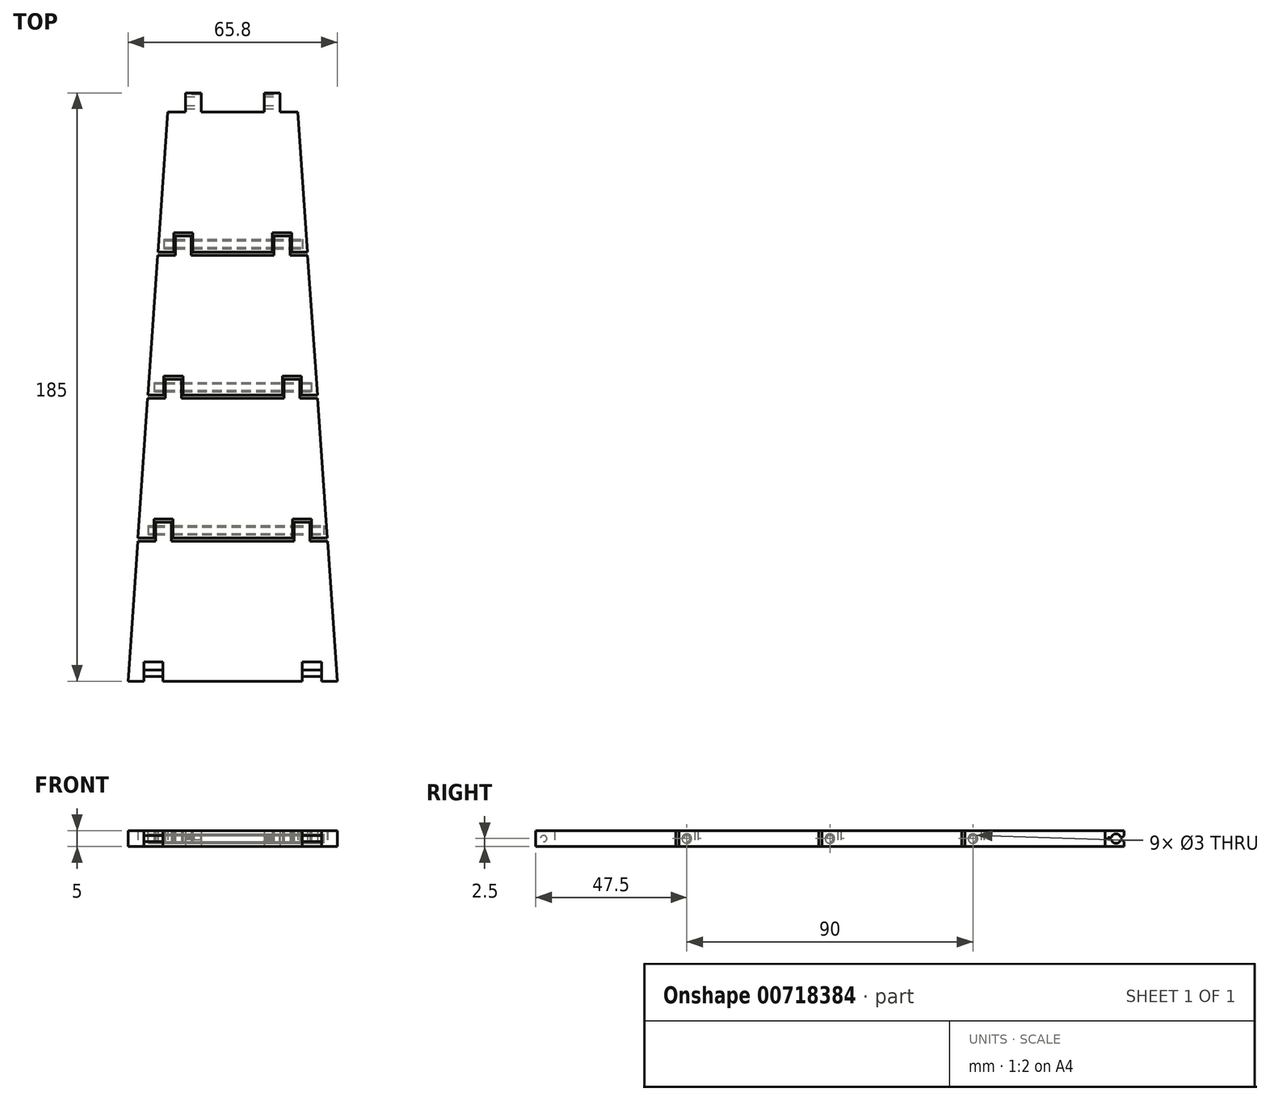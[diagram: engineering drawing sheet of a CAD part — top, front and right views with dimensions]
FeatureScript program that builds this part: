
annotation { "Feature Type Name" : "Feature", "Feature Type Description" : "" }
export const myFeature = defineFeature(function(context is Context, id is Id, definition is map)
    precondition{}
    {
        {
            var Q0;
            Q0=qCreatedBy(makeId("Top.planeOp"),FACE);
            var sketch = newSketch(context, id + "F0", { "sketchPlane" : qUnion([Q0])});
            skLineSegment(sketch, "E0", {"start": v(-23.52, 43.1) * mm, "end": v(-18.52, 43.1) * mm});
            skLineSegment(sketch, "E1", {"start": v(-26.65, -1.9) * mm, "end": v(-21.65, -1.9) * mm});
            skLineSegment(sketch, "E2", {"start": v(-29.78, -46.9) * mm, "end": v(-24.78, -46.9) * mm});
            skLineSegment(sketch, "E3", {"start": v(-32.9, -91.9) * mm, "end": v(-27.9, -91.9) * mm});
            skLineSegment(sketch, "E4.top", {"start": v(-18.52, 49.1) * mm, "end": v(-12.52, 49.1) * mm});
            skLineSegment(sketch, "E4.left", {"start": v(-18.52, 43.1) * mm, "end": v(-18.52, 49.1) * mm});
            skLineSegment(sketch, "E4.right", {"start": v(-12.52, 43.1) * mm, "end": v(-12.52, 49.1) * mm});
            skLineSegment(sketch, "E5.top", {"start": v(-21.65, 4.1) * mm, "end": v(-15.65, 4.1) * mm});
            skLineSegment(sketch, "E5.left", {"start": v(-21.65, -1.9) * mm, "end": v(-21.65, 4.1) * mm});
            skLineSegment(sketch, "E5.right", {"start": v(-15.65, -1.9) * mm, "end": v(-15.65, 4.1) * mm});
            skLineSegment(sketch, "E6.top", {"start": v(-24.78, -40.9) * mm, "end": v(-18.78, -40.9) * mm});
            skLineSegment(sketch, "E6.left", {"start": v(-24.78, -46.9) * mm, "end": v(-24.78, -40.9) * mm});
            skLineSegment(sketch, "E6.right", {"start": v(-18.78, -46.9) * mm, "end": v(-18.78, -40.9) * mm});
            skLineSegment(sketch, "E7.top", {"start": v(-27.9, -85.9) * mm, "end": v(-21.9, -85.9) * mm});
            skLineSegment(sketch, "E7.left", {"start": v(-27.9, -91.9) * mm, "end": v(-27.9, -85.9) * mm});
            skLineSegment(sketch, "E7.right", {"start": v(-21.9, -91.9) * mm, "end": v(-21.9, -85.9) * mm});
            skLineSegment(sketch, "E8.MirrorCS", {"start": v(27.9, -91.9) * mm, "end": v(27.9, -85.9) * mm});
            skLineSegment(sketch, "E9.MirrorCS", {"start": v(27.9, -85.9) * mm, "end": v(21.9, -85.9) * mm});
            skLineSegment(sketch, "E10.MirrorCS", {"start": v(21.9, -91.9) * mm, "end": v(21.9, -85.9) * mm});
            skLineSegment(sketch, "E11.MirrorCS", {"start": v(24.78, -46.9) * mm, "end": v(24.78, -40.9) * mm});
            skLineSegment(sketch, "E12.MirrorCS", {"start": v(18.78, -46.9) * mm, "end": v(18.78, -40.9) * mm});
            skLineSegment(sketch, "E13.MirrorCS", {"start": v(24.78, -40.9) * mm, "end": v(18.78, -40.9) * mm});
            skLineSegment(sketch, "E14.MirrorCS", {"start": v(21.65, 4.1) * mm, "end": v(15.65, 4.1) * mm});
            skLineSegment(sketch, "E15.MirrorCS", {"start": v(21.65, -1.9) * mm, "end": v(21.65, 4.1) * mm});
            skLineSegment(sketch, "E16.MirrorCS", {"start": v(15.65, -1.9) * mm, "end": v(15.65, 4.1) * mm});
            skLineSegment(sketch, "E17.MirrorCS", {"start": v(12.52, 43.1) * mm, "end": v(12.52, 49.1) * mm});
            skLineSegment(sketch, "E18.MirrorCS", {"start": v(18.52, 49.1) * mm, "end": v(12.52, 49.1) * mm});
            skLineSegment(sketch, "E19.MirrorCS", {"start": v(18.52, 43.1) * mm, "end": v(18.52, 49.1) * mm});
            skLineSegment(sketch, "E20", {"start": v(-20.46, 87.1) * mm, "end": v(-14.89, 87.1) * mm});
            skLineSegment(sketch, "E21", {"start": v(-23.59, 42.1) * mm, "end": v(-18.02, 42.1) * mm});
            skLineSegment(sketch, "E22", {"start": v(-26.72, -2.9) * mm, "end": v(-21.15, -2.9) * mm});
            skLineSegment(sketch, "E23", {"start": v(-29.84, -47.9) * mm, "end": v(-24.28, -47.9) * mm});
            skLineSegment(sketch, "E24.top", {"start": v(-14.89, 93.1) * mm, "end": v(-9.89, 93.1) * mm});
            skLineSegment(sketch, "E24.left", {"start": v(-14.89, 87.1) * mm, "end": v(-14.89, 93.1) * mm});
            skLineSegment(sketch, "E24.right", {"start": v(-9.89, 87.1) * mm, "end": v(-9.89, 93.1) * mm});
            skLineSegment(sketch, "E25.top", {"start": v(-18.02, 48.1) * mm, "end": v(-13.02, 48.1) * mm});
            skLineSegment(sketch, "E25.left", {"start": v(-18.02, 42.1) * mm, "end": v(-18.02, 48.1) * mm});
            skLineSegment(sketch, "E25.right", {"start": v(-13.02, 42.1) * mm, "end": v(-13.02, 48.1) * mm});
            skLineSegment(sketch, "E26.top", {"start": v(-21.15, 3.1) * mm, "end": v(-16.15, 3.1) * mm});
            skLineSegment(sketch, "E26.left", {"start": v(-21.15, -2.9) * mm, "end": v(-21.15, 3.1) * mm});
            skLineSegment(sketch, "E26.right", {"start": v(-16.15, -2.9) * mm, "end": v(-16.15, 3.1) * mm});
            skLineSegment(sketch, "E27.top", {"start": v(-24.28, -41.9) * mm, "end": v(-19.28, -41.9) * mm});
            skLineSegment(sketch, "E27.left", {"start": v(-24.28, -47.9) * mm, "end": v(-24.28, -41.9) * mm});
            skLineSegment(sketch, "E27.right", {"start": v(-19.28, -47.9) * mm, "end": v(-19.28, -41.9) * mm});
            skLineSegment(sketch, "E28.MirrorCS", {"start": v(14.89, 93.1) * mm, "end": v(9.89, 93.1) * mm});
            skLineSegment(sketch, "E29.MirrorCS", {"start": v(18.02, 42.1) * mm, "end": v(18.02, 48.1) * mm});
            skLineSegment(sketch, "E30.MirrorCS", {"start": v(18.02, 48.1) * mm, "end": v(13.02, 48.1) * mm});
            skLineSegment(sketch, "E31.MirrorCS", {"start": v(13.02, 42.1) * mm, "end": v(13.02, 48.1) * mm});
            skLineSegment(sketch, "E32.MirrorCS", {"start": v(21.15, -2.9) * mm, "end": v(21.15, 3.1) * mm});
            skLineSegment(sketch, "E33.MirrorCS", {"start": v(21.15, 3.1) * mm, "end": v(16.15, 3.1) * mm});
            skLineSegment(sketch, "E34.MirrorCS", {"start": v(16.15, -2.9) * mm, "end": v(16.15, 3.1) * mm});
            skLineSegment(sketch, "E35.MirrorCS", {"start": v(24.28, -47.9) * mm, "end": v(24.28, -41.9) * mm});
            skLineSegment(sketch, "E36.MirrorCS", {"start": v(24.28, -41.9) * mm, "end": v(19.28, -41.9) * mm});
            skLineSegment(sketch, "E37.MirrorCS", {"start": v(19.28, -47.9) * mm, "end": v(19.28, -41.9) * mm});
            skLineSegment(sketch, "E38.trimOffspring", {"start": v(-20.46, 87.1) * mm, "end": v(-23.52, 43.1) * mm});
            skLineSegment(sketch, "E39.trimOffspring", {"start": v(14.89, 87.1) * mm, "end": v(20.46, 87.1) * mm});
            skLineSegment(sketch, "E40.trimOffspring", {"start": v(20.46, 87.1) * mm, "end": v(23.52, 43.1) * mm});
            skLineSegment(sketch, "E41.trimOffspring", {"start": v(-9.89, 87.1) * mm, "end": v(9.89, 87.1) * mm});
            skLineSegment(sketch, "E42.trimOffspring", {"start": v(-23.59, 42.1) * mm, "end": v(-26.65, -1.9) * mm});
            skLineSegment(sketch, "E43.trimOffspring", {"start": v(-12.52, 43.1) * mm, "end": v(12.52, 43.1) * mm});
            skLineSegment(sketch, "E44.trimOffspring", {"start": v(-13.02, 42.1) * mm, "end": v(13.02, 42.1) * mm});
            skLineSegment(sketch, "E45.trimOffspring", {"start": v(18.52, 43.1) * mm, "end": v(23.52, 43.1) * mm});
            skLineSegment(sketch, "E46.trimOffspring", {"start": v(18.02, 42.1) * mm, "end": v(23.59, 42.1) * mm});
            skLineSegment(sketch, "E47.trimOffspring", {"start": v(23.59, 42.1) * mm, "end": v(26.65, -1.9) * mm});
            skLineSegment(sketch, "E48.trimOffspring", {"start": v(-26.72, -2.9) * mm, "end": v(-29.78, -46.9) * mm});
            skLineSegment(sketch, "E49.trimOffspring", {"start": v(-15.65, -1.9) * mm, "end": v(15.65, -1.9) * mm});
            skLineSegment(sketch, "E50.trimOffspring", {"start": v(-16.15, -2.9) * mm, "end": v(16.15, -2.9) * mm});
            skLineSegment(sketch, "E51.trimOffspring", {"start": v(21.65, -1.9) * mm, "end": v(26.65, -1.9) * mm});
            skLineSegment(sketch, "E52.trimOffspring", {"start": v(21.15, -2.9) * mm, "end": v(26.72, -2.9) * mm});
            skLineSegment(sketch, "E53.trimOffspring", {"start": v(26.72, -2.9) * mm, "end": v(29.78, -46.9) * mm});
            skLineSegment(sketch, "E54.trimOffspring", {"start": v(-29.84, -47.9) * mm, "end": v(-32.9, -91.9) * mm});
            skLineSegment(sketch, "E55.trimOffspring", {"start": v(-18.78, -46.9) * mm, "end": v(18.78, -46.9) * mm});
            skLineSegment(sketch, "E56.trimOffspring", {"start": v(-19.28, -47.9) * mm, "end": v(19.28, -47.9) * mm});
            skLineSegment(sketch, "E57.trimOffspring", {"start": v(24.78, -46.9) * mm, "end": v(29.78, -46.9) * mm});
            skLineSegment(sketch, "E58.trimOffspring", {"start": v(24.28, -47.9) * mm, "end": v(29.84, -47.9) * mm});
            skLineSegment(sketch, "E59.trimOffspring", {"start": v(29.84, -47.9) * mm, "end": v(32.9, -91.9) * mm});
            skLineSegment(sketch, "E60.trimOffspring", {"start": v(-21.9, -91.9) * mm, "end": v(21.9, -91.9) * mm});
            skLineSegment(sketch, "E61.trimOffspring", {"start": v(27.9, -91.9) * mm, "end": v(32.9, -91.9) * mm});
            skLineSegment(sketch, "E62", {"start": v(9.89, 93.1) * mm, "end": v(9.89, 87.1) * mm});
            skLineSegment(sketch, "E63", {"start": v(14.89, 93.1) * mm, "end": v(14.89, 87.1) * mm});
            skSolve(sketch);
        }
        {
            var Q0;
            Q0 = qSketchRegion(id + "F0", true);
            extrude(context, id + "F1", {"entities" : qUnion([Q0]), "depth" : 5 * mm, "offsetDistance" : 25 * mm});
        }
        {
            var Q0;
            Q0=makeQuery(id+"F1.opExtrude","SWEPT_FACE",FACE,{"disambiguationData":[OSD([sQuery(id+"F0.wireOp",EDGE,"E29.MirrorCS")])]});
            cPlane(context, id + "F2", {"entities" : qUnion([Q0]), "cplaneType" : CPlaneType.OFFSET, "offset" : 10 * mm, "width" : 150 * mm, "height" : 150 * mm});
        }
        {
            var Q0;
            Q0=makeQuery(id+"F1.opExtrude","SWEPT_FACE",FACE,{"disambiguationData":[OSD([sQuery(id+"F0.wireOp",EDGE,"E32.MirrorCS")])]});
            cPlane(context, id + "F3", {"entities" : qUnion([Q0]), "cplaneType" : CPlaneType.OFFSET, "offset" : 10 * mm, "width" : 150 * mm, "height" : 150 * mm});
        }
        {
            var Q0;
            Q0=makeQuery(id+"F1.opExtrude","SWEPT_FACE",FACE,{"disambiguationData":[OSD([sQuery(id+"F0.wireOp",EDGE,"E35.MirrorCS")])]});
            cPlane(context, id + "F4", {"entities" : qUnion([Q0]), "cplaneType" : CPlaneType.OFFSET, "offset" : 10 * mm, "width" : 150 * mm, "height" : 150 * mm});
        }
        {
            var Q0;
            Q0=makeQuery(id+"F1.opExtrude","SWEPT_FACE",FACE,{"disambiguationData":[OSD([sQuery(id+"F0.wireOp",EDGE,"E10.MirrorCS")])]});
            cPlane(context, id + "F5", {"entities" : qUnion([Q0]), "cplaneType" : CPlaneType.OFFSET, "offset" : 15 * mm, "width" : 150 * mm, "height" : 150 * mm});
        }
        {
            var Q0;
            Q0=makeQuery(id+"F1.opExtrude","SWEPT_FACE",FACE,{"disambiguationData":[OSD([sQuery(id+"F0.wireOp",EDGE,"E63")])]});
            cPlane(context, id + "F6", {"entities" : qUnion([Q0]), "cplaneType" : CPlaneType.OFFSET, "offset" : 10 * mm, "width" : 150 * mm, "height" : 150 * mm});
        }
        {
            var Q0;
            Q0=qCreatedBy(id+"F2.planeOp",FACE);
            var sketch = newSketch(context, id + "F7", { "sketchPlane" : qUnion([Q0])});
            skCircle(sketch, "E64", {"center": v(45.6, 2.5) * mm, "radius": 1.5 * mm});
            skCircle(sketch, "E65", {"center": v(45.6, 2.5) * mm, "radius": 1 * mm});
            skSolve(sketch);
        }
        {
            var Q0;
            Q0=qCreatedBy(id+"F3.planeOp",FACE);
            var sketch = newSketch(context, id + "F8", { "sketchPlane" : qUnion([Q0])});
            skCircle(sketch, "E66", {"center": v(0.6, 2.5) * mm, "radius": 1.5 * mm});
            skCircle(sketch, "E67", {"center": v(0.6, 2.5) * mm, "radius": 1 * mm});
            skSolve(sketch);
        }
        {
            var Q0;
            Q0=qCreatedBy(id+"F4.planeOp",FACE);
            var sketch = newSketch(context, id + "F9", { "sketchPlane" : qUnion([Q0])});
            skCircle(sketch, "E68", {"center": v(-44.4, 2.5) * mm, "radius": 1.5 * mm});
            skCircle(sketch, "E69", {"center": v(-44.4, 2.5) * mm, "radius": 1 * mm});
            skSolve(sketch);
        }
        {
            var Q0;
            Q0=qCreatedBy(id+"F5.planeOp",FACE);
            var sketch = newSketch(context, id + "F10", { "sketchPlane" : qUnion([Q0])});
            skCircle(sketch, "E70", {"center": v(-89.4, 2.5) * mm, "radius": 1 * mm});
            skSolve(sketch);
        }
        {
            var Q0;
            Q0=qCreatedBy(id+"F6.planeOp",FACE);
            var sketch = newSketch(context, id + "F11", { "sketchPlane" : qUnion([Q0])});
            skArc(sketch, "E71", {"start": v(92.01, 3) * mm, "mid": v(90.47, 4) * mm, "end": v(89.12, 2.75) * mm});
            skLineSegment(sketch, "E72.bottom", {"start": v(95.6, 3) * mm, "end": v(92.01, 3) * mm});
            skLineSegment(sketch, "E72.top", {"start": v(95.6, 2) * mm, "end": v(92.01, 2) * mm});
            skLineSegment(sketch, "E72.left", {"start": v(95.6, 3) * mm, "end": v(95.6, 2) * mm});
            skPoint(sketch, "E73.orphan", {"position": v(90.6, 2) * mm});
            skLineSegment(sketch, "E74.bottom", {"start": v(89.12, 2.75) * mm, "end": v(88.1, 2.75) * mm});
            skLineSegment(sketch, "E74.top", {"start": v(89.12, 2.25) * mm, "end": v(88.1, 2.25) * mm});
            skLineSegment(sketch, "E74.right", {"start": v(88.1, 2.75) * mm, "end": v(88.1, 2.25) * mm});
            skArc(sketch, "E75.trimOffspring", {"start": v(89.12, 2.25) * mm, "mid": v(90.47, 1) * mm, "end": v(92.01, 2) * mm});
            skSolve(sketch);
        }
        {
            var Q0;
            Q0 = qSketchRegion(id + "F10", true);
            extrude(context, id + "F12", {"entities" : qUnion([Q0]), "operationType" : NewBodyOperationType.ADD, "oppositeDirection" : true, "depth" : 67.7 * mm, "offsetDistance" : 25 * mm, "hasSecondDirection" : true, "secondDirectionOppositeDirection" : true, "secondDirectionDepth" : 5.7 * mm});
        }
        {
            var Q0;
            Q0 = qSketchRegion(id + "F9", true);
            extrude(context, id + "F13", {"entities" : qUnion([Q0]), "operationType" : NewBodyOperationType.REMOVE, "oppositeDirection" : true, "depth" : 60.8 * mm, "offsetDistance" : 25 * mm, "hasSecondDirection" : true, "secondDirectionOppositeDirection" : true, "secondDirectionDepth" : 5.5 * mm});
        }
        {
            var Q0;
            Q0=makeQuery(id+"F9.imprint","IMPRINT",FACE,{"disambiguationData":[TD([[makeQuery(id+"F9.imprint","IMPRINT",EDGE,{"derivedFrom":sQuery(id+"F9.wireOp",EDGE,"E69")}),1.0]])]});
            extrude(context, id + "F14", {"entities" : qUnion([Q0]), "operationType" : NewBodyOperationType.ADD, "oppositeDirection" : true, "depth" : 62.6 * mm, "offsetDistance" : 25 * mm, "hasSecondDirection" : true, "secondDirectionOppositeDirection" : true, "secondDirectionDepth" : 6 * mm});
        }
        {
            var Q0;
            Q0 = qSketchRegion(id + "F8", true);
            extrude(context, id + "F15", {"entities" : qUnion([Q0]), "operationType" : NewBodyOperationType.REMOVE, "oppositeDirection" : true, "depth" : 55.8 * mm, "offsetDistance" : 25 * mm, "hasSecondDirection" : true, "secondDirectionOppositeDirection" : true, "secondDirectionDepth" : 6.3 * mm});
        }
        {
            var Q0;
            Q0=makeQuery(id+"F8.imprint","IMPRINT",FACE,{"disambiguationData":[TD([[makeQuery(id+"F8.imprint","IMPRINT",EDGE,{"derivedFrom":sQuery(id+"F8.wireOp",EDGE,"E67")}),1.0]])]});
            var Q1;
            Q1=sQuery(id+"F8.wireOp",EDGE,"E67");
            extrude(context, id + "F16", {"entities" : qUnion([Q0]), "operationType" : NewBodyOperationType.ADD, "surfaceOperationType" : NewSurfaceOperationType.ADD, "surfaceEntities" : qUnion([Q1]), "oppositeDirection" : true, "depth" : 54.7 * mm, "offsetDistance" : 25 * mm, "hasSecondDirection" : true, "secondDirectionOppositeDirection" : true, "secondDirectionDepth" : 5.7 * mm});
        }
        {
            var Q0;
            Q0 = qSketchRegion(id + "F7", true);
            extrude(context, id + "F17", {"entities" : qUnion([Q0]), "operationType" : NewBodyOperationType.REMOVE, "oppositeDirection" : true, "depth" : 49.6 * mm, "offsetDistance" : 25 * mm, "hasSecondDirection" : true, "secondDirectionOppositeDirection" : true, "secondDirectionDepth" : 6 * mm});
        }
        {
            var Q0;
            Q0=makeQuery(id+"F7.imprint","IMPRINT",FACE,{"disambiguationData":[TD([[makeQuery(id+"F7.imprint","IMPRINT",EDGE,{"derivedFrom":sQuery(id+"F7.wireOp",EDGE,"E65")}),1.0]])]});
            extrude(context, id + "F18", {"entities" : qUnion([Q0]), "operationType" : NewBodyOperationType.ADD, "oppositeDirection" : true, "depth" : 48 * mm, "offsetDistance" : 25 * mm, "hasSecondDirection" : true, "secondDirectionOppositeDirection" : true, "secondDirectionDepth" : 5.7 * mm});
        }
        {
            var Q0;
            Q0 = qSketchRegion(id + "F11", true);
            extrude(context, id + "F19", {"entities" : qUnion([Q0]), "operationType" : NewBodyOperationType.REMOVE, "oppositeDirection" : true, "depth" : 45.5 * mm, "offsetDistance" : 25 * mm});
        }
        {
            var Q0;
            Q0=makeQuery(id+"F19.boolean.opBoolean","INTERSECT",EDGE,{"derivedFrom":[makeQuery(id+"F1.opExtrude","SWEPT_FACE",FACE,{"disambiguationData":[OSD([sQuery(id+"F0.wireOp",EDGE,"E24.top")])]}),makeQuery(id+"F19.opExtrude","SWEPT_FACE",FACE,{"disambiguationData":[OSD([sQuery(id+"F11.wireOp",EDGE,"E72.bottom")])]})]});
            var Q1;
            Q1=makeQuery(id+"F19.boolean.opBoolean","INTERSECT",EDGE,{"derivedFrom":[makeQuery(id+"F1.opExtrude","SWEPT_FACE",FACE,{"disambiguationData":[OSD([sQuery(id+"F0.wireOp",EDGE,"E24.top")])]}),makeQuery(id+"F19.opExtrude","SWEPT_FACE",FACE,{"disambiguationData":[OSD([sQuery(id+"F11.wireOp",EDGE,"E72.top")])]})]});
            var Q2;
            Q2=makeQuery(id+"F19.boolean.opBoolean","INTERSECT",EDGE,{"derivedFrom":[makeQuery(id+"F1.opExtrude","SWEPT_FACE",FACE,{"disambiguationData":[OSD([sQuery(id+"F0.wireOp",EDGE,"E28.MirrorCS")])]}),makeQuery(id+"F19.opExtrude","SWEPT_FACE",FACE,{"disambiguationData":[OSD([sQuery(id+"F11.wireOp",EDGE,"E72.bottom")])]})]});
            var Q3;
            Q3=makeQuery(id+"F19.boolean.opBoolean","INTERSECT",EDGE,{"derivedFrom":[makeQuery(id+"F1.opExtrude","SWEPT_FACE",FACE,{"disambiguationData":[OSD([sQuery(id+"F0.wireOp",EDGE,"E28.MirrorCS")])]}),makeQuery(id+"F19.opExtrude","SWEPT_FACE",FACE,{"disambiguationData":[OSD([sQuery(id+"F11.wireOp",EDGE,"E72.top")])]})]});
            chamfer(context, id + "F20", {"entities" : qUnion([Q0, Q1, Q2, Q3]), "width" : 0.5 * mm, "tangentPropagation" : true});
        }
    });
